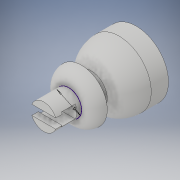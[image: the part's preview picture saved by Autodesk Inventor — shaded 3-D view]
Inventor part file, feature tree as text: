
AUTODESK INVENTOR PART (.ipt)
format: ipt  version: 2018 (Build 220112000, 112)  size: 191,488 bytes
history: native  units: mm
features: sketch x11, extrude x10, fillet x2
ambient origin geometry x8: Origin, YZ Plane, XZ Plane, XY Plane, X Axis, Y Axis, Z Axis, Center Point
bodies: Volumenkörper1 (feature_tree)
feature tree (23):
  extrude  "Extrusion1"  Depth=2.0mm TaperAngle=0.0deg
  fillet  "Rundung1"  Radius=2.0mm
  extrude  "Extrusion2"  Depth=5.0mm TaperAngle=0.0deg
  extrude  "Extrusion3"  Depth=5.0mm TaperAngle=0.0deg
  extrude  "Extrusion5"  Depth=2.0mm TaperAngle=0.0deg
  extrude  "Extrusion6"  Depth=2.0mm TaperAngle=0.0deg
  extrude  "Extrusion7"  Depth=1.1mm TaperAngle=0.0deg
  fillet  "Rundung2"  Radius=5.0mm
  sketch  "Skizze11"  dims[d23=4.0mm d24=4.0mm]
  extrude  "Extrusion8"  Depth=4.0mm
  extrude  "Extrusion9"  Depth=2.15mm TaperAngle=0.0deg
  extrude  "Extrusion10"  Depth=1.0mm TaperAngle=0.0deg
  extrude  "Extrusion11"  [1 undecoded]
  sketch  "Skizze1"  dims[d0=8.0mm d1=2.0mm d2=0.0mm d3=2.0mm]
  sketch  "Skizze2"  dims[d4=5.0mm d5=1.5mm d6=0.0mm]
  sketch  "Skizze3"  dims[d7=10.0mm d8=5.0mm d9=0.0mm]
  sketch  "Skizze5"  dims[d13=10.0mm d14=2.0mm d15=0.0mm]
  sketch  "Skizze6"  dims[d16=8.5mm d17=2.0mm d18=0.0mm]
  sketch  "Skizze8"  dims[d19=1.6mm d20=1.1mm d21=0.0mm d22=5.0mm]
  sketch  "Skizze12"  dims[d25=2.85mm d26=0.0mm d27=2.15mm d28=0.0mm]
  sketch  "Skizze13"  dims[d29=4.0mm d30=1.0mm d31=0.0mm]
  sketch  "Skizze14"  dims[d32=1.0mm d33=0.0mm]
  sketch  "Skizze15"
note: 1 required parameter value undecoded (feature->parameter linkage not recoverable at this tier; creation-order binding heuristic only, values carry confidence <= 0.55)
